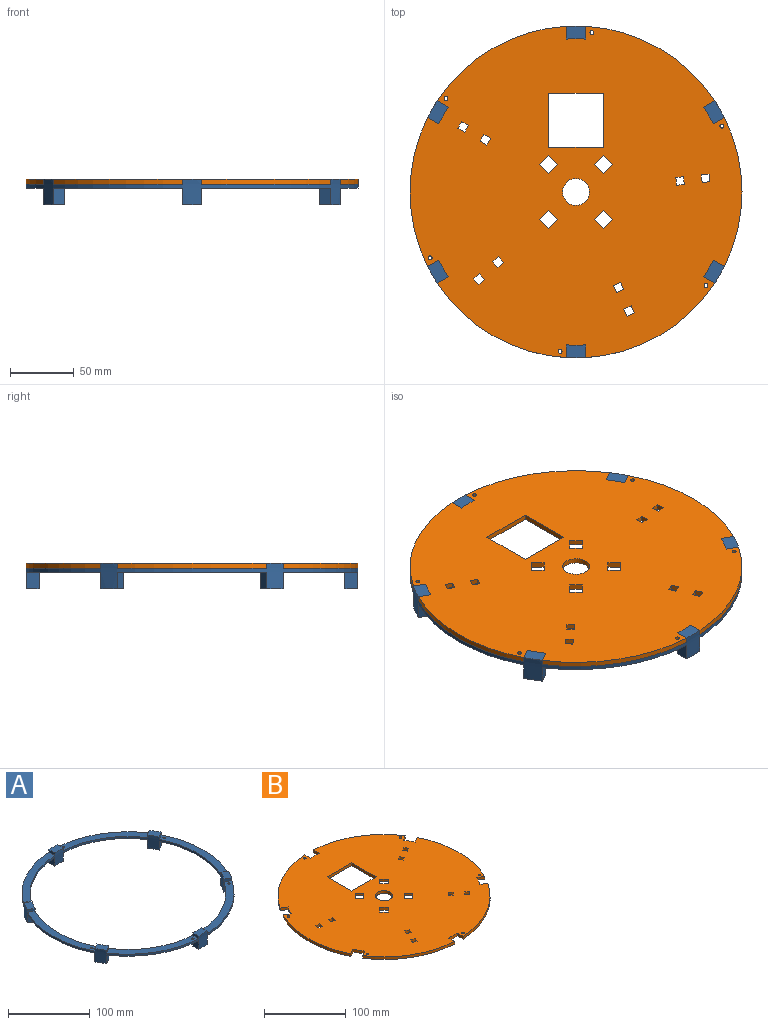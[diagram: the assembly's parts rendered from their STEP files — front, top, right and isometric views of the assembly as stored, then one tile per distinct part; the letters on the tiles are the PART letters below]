
ASSEMBLY  parts=2 mates=1
PART A: 56 faces, bbox 260x260x20 mm
  f0: cylinder r=120mm len=240mm, axis (0,0,-1), area 3792.9mm2, adj f3,f4,f5,f6,f8,f9,f10,f12
  f1: cylinder r=130mm len=260mm, axis (0,0,-1), area 3981.3mm2, adj f3,f4,f5,f6,f8,f9,f10,f12
  f2: cylinder r=1.55mm len=3.1mm, axis (0,0,-1), area 29.2mm2, adj f3,f4
  f3: plane 101.15x63.41mm, normal (0,0,1), area 1151.4mm2, adj f0,f1,f2,f5,f6
  f4: plane 101.15x63.41mm, normal (0,0,-1), area 1151.4mm2, adj f0,f1,f2,f27,f53
  f5: plane 8.68x5.01mm, normal (-0.5,0.87,0), area 40.1mm2, adj f0,f1,f3,f29
  f6: plane 10.02x4mm, normal (1,0,0), area 40.1mm2, adj f0,f1,f3,f54
  f7: cylinder r=1.55mm len=3.1mm, axis (0,0,-1), area 29.2mm2, adj f8,f9
  f8: plane 101.15x63.41mm, normal (0,0,1), area 1151.4mm2, adj f0,f1,f7,f10,f51
  f9: plane 101.15x63.41mm, normal (0,0,-1), area 1151.4mm2, adj f0,f1,f7,f48,f52
  f10: plane 8.68x5.01mm, normal (0.5,0.87,0), area 40.1mm2, adj f0,f1,f8,f49
  f11: cylinder r=1.55mm len=3.1mm, axis (0,0,-1), area 29.2mm2, adj f12,f13
  f12: plane 116.79x22.53mm, normal (0,0,1), area 1151.4mm2, adj f0,f1,f11,f14,f46
  f13: plane 116.79x22.53mm, normal (0,0,-1), area 1151.4mm2, adj f0,f1,f11,f43,f47
  f14: plane 8.68x5.01mm, normal (-0.5,0.87,0), area 40.1mm2, adj f0,f1,f12,f44
  f15: cylinder r=1.55mm len=3.1mm, axis (0,0,-1), area 29.2mm2, adj f16,f17
  f16: plane 101.15x63.41mm, normal (0,0,1), area 1151.4mm2, adj f0,f1,f15,f18,f41
  f17: plane 101.15x63.41mm, normal (0,0,-1), area 1151.4mm2, adj f0,f1,f15,f38,f42
  f18: plane 10.02x4mm, normal (-1,0,0), area 40.1mm2, adj f0,f1,f16,f39
  f19: cylinder r=1.55mm len=3.1mm, axis (0,0,-1), area 29.2mm2, adj f20,f21
  f20: plane 101.15x63.41mm, normal (0,0,1), area 1151.4mm2, adj f0,f1,f19,f22,f36
  f21: plane 101.15x63.41mm, normal (0,0,-1), area 1151.4mm2, adj f0,f1,f19,f33,f37
  f22: plane 8.68x5.01mm, normal (-0.5,-0.87,0), area 40.1mm2, adj f0,f1,f20,f34
  f23: cylinder r=1.55mm len=3.1mm, axis (0,0,-1), area 29.2mm2, adj f24,f25
  f24: plane 116.79x22.53mm, normal (0,0,1), area 1151.4mm2, adj f0,f1,f23,f26,f31
  f25: plane 116.79x22.53mm, normal (0,0,-1), area 1151.4mm2, adj f0,f1,f23,f28,f32
  f26: plane 8.68x5.01mm, normal (0.5,-0.87,0), area 40.1mm2, adj f0,f1,f24,f29
  f27: plane 13x8.68mm, normal (-0.5,0.87,0), area 130.2mm2, adj f0,f1,f4,f30
  f28: plane 13x8.68mm, normal (0.5,-0.87,0), area 130.2mm2, adj f0,f1,f25,f30
  f29: plane 18x16.18mm, normal (0,0,1), area 150.1mm2, adj f0,f1,f5,f26
  f30: plane 18x16.18mm, normal (0,0,-1), area 150.1mm2, adj f0,f1,f27,f28
  f31: plane 8.68x5.01mm, normal (0.5,0.87,0), area 40.1mm2, adj f0,f1,f24,f34
  f32: plane 13x8.68mm, normal (0.5,0.87,0), area 130.2mm2, adj f0,f1,f25,f35
  f33: plane 13x8.68mm, normal (-0.5,-0.87,0), area 130.2mm2, adj f0,f1,f21,f35
  f34: plane 18x16.18mm, normal (0,0,1), area 150.1mm2, adj f0,f1,f22,f31
  f35: plane 18x16.18mm, normal (0,0,-1), area 150.1mm2, adj f0,f1,f32,f33
  f36: plane 10.02x4mm, normal (1,0,0), area 40.1mm2, adj f0,f1,f20,f39
  f37: plane 13x10.02mm, normal (1,0,0), area 130.2mm2, adj f0,f1,f21,f40
  f38: plane 13x10.02mm, normal (-1,0,0), area 130.2mm2, adj f0,f1,f17,f40
  f39: plane 15x10.23mm, normal (0,0,1), area 150.1mm2, adj f0,f1,f18,f36
  f40: plane 15x10.23mm, normal (0,0,-1), area 150.1mm2, adj f0,f1,f37,f38
  f41: plane 8.68x5.01mm, normal (0.5,-0.87,0), area 40.1mm2, adj f0,f1,f16,f44
  f42: plane 13x8.68mm, normal (0.5,-0.87,0), area 130.2mm2, adj f0,f1,f17,f45
  f43: plane 13x8.68mm, normal (-0.5,0.87,0), area 130.2mm2, adj f0,f1,f13,f45
  f44: plane 18x16.18mm, normal (0,0,1), area 150.1mm2, adj f0,f1,f14,f41
  f45: plane 18x16.18mm, normal (0,0,-1), area 150.1mm2, adj f0,f1,f42,f43
  f46: plane 8.68x5.01mm, normal (-0.5,-0.87,0), area 40.1mm2, adj f0,f1,f12,f49
  f47: plane 13x8.68mm, normal (-0.5,-0.87,0), area 130.2mm2, adj f0,f1,f13,f50
  f48: plane 13x8.68mm, normal (0.5,0.87,0), area 130.2mm2, adj f0,f1,f9,f50
  f49: plane 18x16.18mm, normal (0,0,1), area 150.1mm2, adj f0,f1,f10,f46
  f50: plane 18x16.18mm, normal (0,0,-1), area 150.1mm2, adj f0,f1,f47,f48
  f51: plane 10.02x4mm, normal (-1,0,0), area 40.1mm2, adj f0,f1,f8,f54
  f52: plane 13x10.02mm, normal (-1,0,0), area 130.2mm2, adj f0,f1,f9,f55
  f53: plane 13x10.02mm, normal (1,0,0), area 130.2mm2, adj f0,f1,f4,f55
  f54: plane 15x10.23mm, normal (0,0,1), area 150.1mm2, adj f0,f1,f6,f51
  f55: plane 15x10.23mm, normal (0,0,-1), area 150.1mm2, adj f0,f1,f52,f53
PART B: 85 faces, bbox 260x259.6x4 mm
  f0: plane 5.28x4mm, normal (-0.5,0.87,0), area 24.4mm2, adj f1,f67,f83,f84
  f1: plane 5.28x4mm, normal (0.87,0.5,0), area 24.4mm2, adj f0,f2,f83,f84
  f2: plane 5.28x4mm, normal (0.5,-0.87,0), area 24.4mm2, adj f1,f67,f83,f84
  f3: plane 4.53x4.08mm, normal (0.67,0.74,0), area 24.4mm2, adj f4,f68,f83,f84
  f4: plane 4.53x4.08mm, normal (0.74,-0.67,0), area 24.4mm2, adj f3,f5,f83,f84
  f5: plane 4.53x4.08mm, normal (-0.67,-0.74,0), area 24.4mm2, adj f4,f68,f83,f84
  f6: plane 5.57x4mm, normal (0.91,-0.41,0), area 24.4mm2, adj f7,f69,f83,f84
  f7: plane 5.57x4mm, normal (-0.41,-0.91,0), area 24.4mm2, adj f6,f8,f83,f84
  f8: plane 5.57x4mm, normal (-0.91,0.41,0), area 24.4mm2, adj f7,f69,f83,f84
  f9: plane 6.07x4mm, normal (-0.1,-0.99,0), area 24.4mm2, adj f10,f70,f83,f84
  f10: plane 6.07x4mm, normal (-0.99,0.1,0), area 24.4mm2, adj f9,f11,f83,f84
  f11: plane 6.07x4mm, normal (0.1,0.99,0), area 24.4mm2, adj f10,f70,f83,f84
  f12: plane 42.5x4mm, normal (0,-1,0), area 170mm2, adj f13,f71,f83,f84
  f13: plane 42.5x4mm, normal (-1,0,0), area 170mm2, adj f12,f14,f83,f84
  f14: plane 42.5x4mm, normal (0,1,0), area 170mm2, adj f13,f71,f83,f84
  f15: plane 7.07x7.07mm, normal (-0.71,-0.71,0), area 40mm2, adj f16,f72,f83,f84
  f16: plane 7.07x7.07mm, normal (-0.71,0.71,0), area 40mm2, adj f15,f17,f83,f84
  f17: plane 7.07x7.07mm, normal (0.71,0.71,0), area 40mm2, adj f16,f72,f83,f84
  f18: plane 7.07x7.07mm, normal (-0.71,0.71,0), area 40mm2, adj f19,f73,f83,f84
  f19: plane 7.07x7.07mm, normal (0.71,0.71,0), area 40mm2, adj f18,f20,f83,f84
  f20: plane 7.07x7.07mm, normal (0.71,-0.71,0), area 40mm2, adj f19,f73,f83,f84
  f21: cylinder r=120mm len=12.99mm, axis (0,0,-1), area 60mm2, adj f22,f74,f83,f84
  f22: plane 8.68x5.01mm, normal (0.5,-0.87,0), area 40.1mm2, adj f21,f23,f83,f84
  f23: cylinder r=130mm len=101.15mm, axis (0,0,-1), area 484.5mm2, adj f22,f24,f83,f84
  f24: plane 10.02x4mm, normal (-1,0,0), area 40.1mm2, adj f23,f25,f83,f84
  f25: cylinder r=120mm len=15mm, axis (0,0,-1), area 60mm2, adj f24,f26,f83,f84
  f26: plane 10.02x4mm, normal (1,0,0), area 40.1mm2, adj f25,f27,f83,f84
  f27: cylinder r=130mm len=101.15mm, axis (0,0,-1), area 484.5mm2, adj f26,f28,f83,f84
  f28: plane 8.68x5.01mm, normal (-0.5,-0.87,0), area 40.1mm2, adj f27,f29,f83,f84
  f29: cylinder r=120mm len=12.99mm, axis (0,0,-1), area 60mm2, adj f28,f30,f83,f84
  f30: plane 8.68x5.01mm, normal (0.5,0.87,0), area 40.1mm2, adj f29,f31,f83,f84
  f31: cylinder r=130mm len=116.79mm, axis (0,0,-1), area 484.5mm2, adj f30,f32,f83,f84
  f32: plane 8.68x5.01mm, normal (0.5,-0.87,0), area 40.1mm2, adj f31,f33,f83,f84
  f33: cylinder r=120mm len=12.99mm, axis (0,0,-1), area 60mm2, adj f32,f34,f83,f84
  f34: plane 8.68x5.01mm, normal (-0.5,0.87,0), area 40.1mm2, adj f33,f35,f83,f84
  f35: cylinder r=130mm len=101.15mm, axis (0,0,-1), area 484.5mm2, adj f34,f36,f83,f84
  f36: plane 10.02x4mm, normal (1,0,0), area 40.1mm2, adj f35,f37,f83,f84
  f37: cylinder r=120mm len=15mm, axis (0,0,-1), area 60mm2, adj f36,f38,f83,f84
  f38: plane 10.02x4mm, normal (-1,0,0), area 40.1mm2, adj f37,f39,f83,f84
  f39: cylinder r=130mm len=101.15mm, axis (0,0,-1), area 484.5mm2, adj f38,f40,f83,f84
  f40: plane 8.68x5.01mm, normal (0.5,0.87,0), area 40.1mm2, adj f39,f41,f83,f84
  f41: cylinder r=120mm len=12.99mm, axis (0,0,-1), area 60mm2, adj f40,f42,f83,f84
  f42: plane 8.68x5.01mm, normal (-0.5,-0.87,0), area 40.1mm2, adj f41,f43,f83,f84
  f43: cylinder r=130mm len=116.79mm, axis (0,0,-1), area 484.5mm2, adj f42,f74,f83,f84
  f44: plane 7.07x7.07mm, normal (-0.71,0.71,0), area 40mm2, adj f45,f75,f83,f84
  f45: plane 7.07x7.07mm, normal (0.71,0.71,0), area 40mm2, adj f44,f46,f83,f84
  f46: plane 7.07x7.07mm, normal (0.71,-0.71,0), area 40mm2, adj f45,f75,f83,f84
  f47: plane 7.07x7.07mm, normal (0.71,-0.71,0), area 40mm2, adj f48,f76,f83,f84
  f48: plane 7.07x7.07mm, normal (-0.71,-0.71,0), area 40mm2, adj f47,f49,f83,f84
  f49: plane 7.07x7.07mm, normal (-0.71,0.71,0), area 40mm2, adj f48,f76,f83,f84
  f50: plane 6.07x4mm, normal (-0.1,-0.99,0), area 24.4mm2, adj f51,f77,f83,f84
  f51: plane 6.07x4mm, normal (-0.99,0.1,0), area 24.4mm2, adj f50,f52,f83,f84
  f52: plane 6.07x4mm, normal (0.1,0.99,0), area 24.4mm2, adj f51,f77,f83,f84
  f53: plane 5.57x4mm, normal (0.91,-0.41,0), area 24.4mm2, adj f54,f78,f83,f84
  f54: plane 5.57x4mm, normal (-0.41,-0.91,0), area 24.4mm2, adj f53,f55,f83,f84
  f55: plane 5.57x4mm, normal (-0.91,0.41,0), area 24.4mm2, adj f54,f78,f83,f84
  f56: plane 4.53x4.08mm, normal (0.67,0.74,0), area 24.4mm2, adj f57,f79,f83,f84
  f57: plane 4.53x4.08mm, normal (0.74,-0.67,0), area 24.4mm2, adj f56,f58,f83,f84
  f58: plane 4.53x4.08mm, normal (-0.67,-0.74,0), area 24.4mm2, adj f57,f79,f83,f84
  f59: plane 5.28x4mm, normal (-0.5,0.87,0), area 24.4mm2, adj f60,f80,f83,f84
  f60: plane 5.28x4mm, normal (0.87,0.5,0), area 24.4mm2, adj f59,f61,f83,f84
  f61: plane 5.28x4mm, normal (0.5,-0.87,0), area 24.4mm2, adj f60,f80,f83,f84
  f62: cylinder r=1.55mm len=4mm, axis (0,0,-1), area 39mm2, adj f83,f84
  f63: cylinder r=1.55mm len=4mm, axis (0,0,-1), area 39mm2, adj f83,f84
  f64: cylinder r=1.55mm len=4mm, axis (0,0,-1), area 39mm2, adj f83,f84
  f65: cylinder r=1.55mm len=4mm, axis (0,0,-1), area 39mm2, adj f83,f84
  f66: cylinder r=1.55mm len=4mm, axis (0,0,-1), area 39mm2, adj f83,f84
  f67: plane 5.28x4mm, normal (-0.87,-0.5,0), area 24.4mm2, adj f0,f2,f83,f84
  f68: plane 4.53x4.08mm, normal (-0.74,0.67,0), area 24.4mm2, adj f3,f5,f83,f84
  f69: plane 5.57x4mm, normal (0.41,0.91,0), area 24.4mm2, adj f6,f8,f83,f84
  f70: plane 6.07x4mm, normal (0.99,-0.1,0), area 24.4mm2, adj f9,f11,f83,f84
  f71: plane 42.5x4mm, normal (1,0,0), area 170mm2, adj f12,f14,f83,f84
  f72: plane 7.07x7.07mm, normal (0.71,-0.71,0), area 40mm2, adj f15,f17,f83,f84
  f73: plane 7.07x7.07mm, normal (-0.71,-0.71,0), area 40mm2, adj f18,f20,f83,f84
  f74: plane 8.68x5.01mm, normal (-0.5,0.87,0), area 40.1mm2, adj f21,f43,f83,f84
  f75: plane 7.07x7.07mm, normal (-0.71,-0.71,0), area 40mm2, adj f44,f46,f83,f84
  f76: plane 7.07x7.07mm, normal (0.71,0.71,0), area 40mm2, adj f47,f49,f83,f84
  f77: plane 6.07x4mm, normal (0.99,-0.1,0), area 24.4mm2, adj f50,f52,f83,f84
  f78: plane 5.57x4mm, normal (0.41,0.91,0), area 24.4mm2, adj f53,f55,f83,f84
  f79: plane 4.53x4.08mm, normal (-0.74,0.67,0), area 24.4mm2, adj f56,f58,f83,f84
  f80: plane 5.28x4mm, normal (-0.87,-0.5,0), area 24.4mm2, adj f59,f61,f83,f84
  f81: cylinder r=10.55mm len=21.1mm, axis (0,0,-1), area 265.2mm2, adj f83,f84
  f82: cylinder r=1.55mm len=4mm, axis (0,0,-1), area 39mm2, adj f83,f84
  f83: plane 260x259.57mm, normal (0,0,1), area 49293.5mm2, adj f0,f1,f2,f3,f4,f5,f6,f7
  f84: plane 260x259.57mm, normal (0,0,-1), area 49293.5mm2, adj f0,f1,f2,f3,f4,f5,f6,f7
PLACE A t=(-2.7,331.78,-22)mm
PLACE B rot(axis=(0,1,0),180deg) t=(-282.7,331.78,-15)mm
MATE fastened B.f62 <-> A.f2  axis (0,0,-1) through (9.8,106.55,-19)mm
